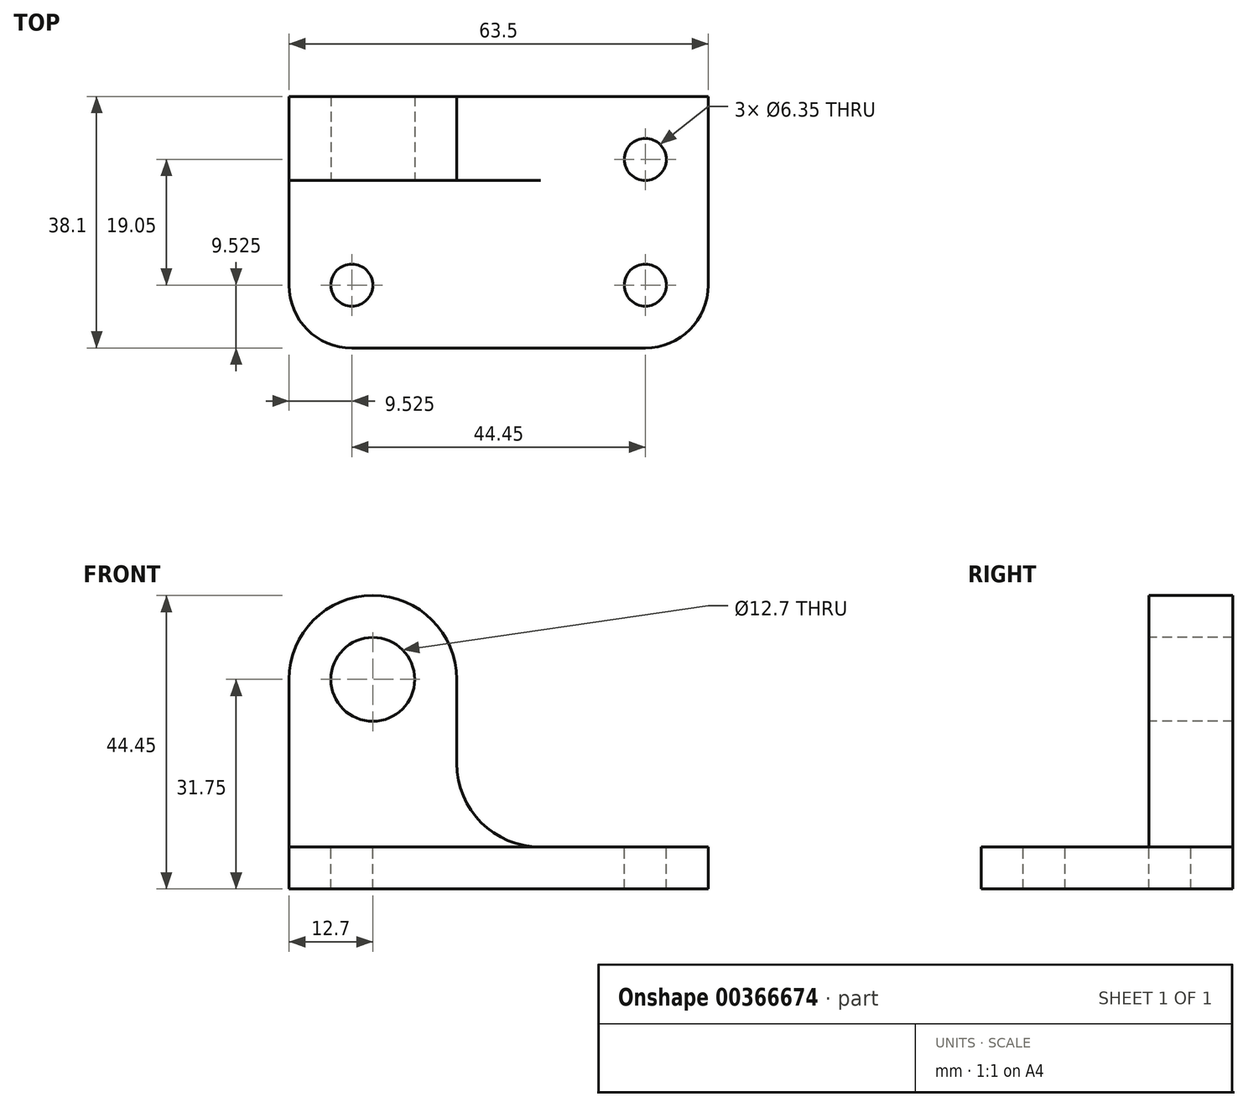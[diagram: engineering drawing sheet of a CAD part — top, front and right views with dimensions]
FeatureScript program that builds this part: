
annotation { "Feature Type Name" : "Feature", "Feature Type Description" : "" }
export const myFeature = defineFeature(function(context is Context, id is Id, definition is map)
    precondition{}
    {
        {
            var Q0;
            Q0=qCreatedBy(makeId("Front.planeOp"),FACE);
            var sketch = newSketch(context, id + "F0", { "sketchPlane" : qUnion([Q0])});
            skLineSegment(sketch, "E0", {"start": v(-70.82, 0) * mm, "end": v(-70.82, 44.45) * mm});
            skLineSegment(sketch, "E1", {"start": v(-70.82, 44.45) * mm, "end": v(-7.32, 44.45) * mm});
            skLineSegment(sketch, "E2", {"start": v(-7.32, 44.45) * mm, "end": v(-7.32, 0) * mm});
            skLineSegment(sketch, "E3", {"start": v(-7.32, 0) * mm, "end": v(-70.82, 0) * mm});
            skSolve(sketch);
        }
        {
            var Q0;
            Q0=makeQuery(id+"F0.imprint","IMPRINT",FACE,{"disambiguationData":[TD([[makeQuery(id+"F0.imprint","IMPRINT",EDGE,{"derivedFrom":sQuery(id+"F0.wireOp",EDGE,"E0")}),-1.0]])]});
            extrude(context, id + "F1", {"entities" : qUnion([Q0]), "depth" : 38.1 * mm});
        }
        {
            var Q0;
            Q0=makeQuery(id+"F1.opExtrude","CAP_FACE",FACE,{"disambiguationData":[OSD([sQuery(id+"F0.wireOp",EDGE,"E0"),sQuery(id+"F0.wireOp",EDGE,"E1"),sQuery(id+"F0.wireOp",EDGE,"E2"),sQuery(id+"F0.wireOp",EDGE,"E3")])],"isStart":false});
            var sketch = newSketch(context, id + "F2", { "sketchPlane" : qUnion([Q0])});
            skLineSegment(sketch, "E4", {"start": v(-70.82, 6.35) * mm, "end": v(-7.32, 6.35) * mm});
            skSolve(sketch);
        }
        {
            var Q0;
            {var subQ0=sQuery(id+"F2.wireOp",EDGE,"E4");Q0=makeQuery(id+"F2.imprint","IMPRINT",FACE,{"disambiguationData":[TD([[makeQuery(id+"F2.imprint","IMPRINT",EDGE,{"derivedFrom":subQ0}),1.0]])]});}
            extrude(context, id + "F3", {"entities" : qUnion([Q0]), "operationType" : NewBodyOperationType.REMOVE, "oppositeDirection" : true, "depth" : 25.4 * mm});
        }
        {
            var Q0;
            Q0=makeQuery(id+"F3.boolean.opBoolean","COPY",FACE,{"derivedFrom":makeQuery(id+"F3.opExtrude","SWEPT_FACE",FACE,{"disambiguationData":[OSD([sQuery(id+"F2.wireOp",EDGE,"E4")])]})});
            var sketch = newSketch(context, id + "F4", { "sketchPlane" : qUnion([Q0])});
            skCircle(sketch, "E5", {"center": v(-61.3, -28.58) * mm, "radius": 3.18 * mm});
            skCircle(sketch, "E6", {"center": v(-16.85, -28.58) * mm, "radius": 3.18 * mm});
            skArc(sketch, "E7", {"start": v(-70.82, -28.58) * mm, "mid": v(-68.03, -35.31) * mm, "end": v(-61.3, -38.1) * mm});
            skArc(sketch, "E8", {"start": v(-16.85, -38.1) * mm, "mid": v(-10.11, -35.3) * mm, "end": v(-7.32, -28.57) * mm});
            skSolve(sketch);
        }
        {
            var Q0;
            {var subQ0=sQuery(id+"F4.wireOp",EDGE,"E7");Q0=makeQuery(id+"F4.imprint","IMPRINT",FACE,{"disambiguationData":[TD([[makeQuery(id+"F4.imprint","IMPRINT",EDGE,{"derivedFrom":subQ0}),-1.0]])]});}
            var Q1;
            Q1=makeQuery(id+"F4.imprint","IMPRINT",FACE,{"disambiguationData":[TD([[makeQuery(id+"F4.imprint","IMPRINT",EDGE,{"derivedFrom":sQuery(id+"F4.wireOp",EDGE,"E5")}),1.0]])]});
            var Q2;
            Q2=makeQuery(id+"F4.imprint","IMPRINT",FACE,{"disambiguationData":[TD([[makeQuery(id+"F4.imprint","IMPRINT",EDGE,{"derivedFrom":sQuery(id+"F4.wireOp",EDGE,"E6")}),1.0]])]});
            var Q3;
            {var subQ0=sQuery(id+"F4.wireOp",EDGE,"E8");Q3=makeQuery(id+"F4.imprint","IMPRINT",FACE,{"disambiguationData":[TD([[makeQuery(id+"F4.imprint","IMPRINT",EDGE,{"derivedFrom":subQ0}),-1.0]])]});}
            extrude(context, id + "F5", {"entities" : qUnion([Q0, Q1, Q2, Q3]), "operationType" : NewBodyOperationType.REMOVE, "oppositeDirection" : true, "depth" : 25.4 * mm});
        }
        {
            var Q0;
            Q0=makeQuery(id+"F3.boolean.opBoolean","COPY",FACE,{"derivedFrom":makeQuery(id+"F3.opExtrude","CAP_FACE",FACE,{"disambiguationData":[OSD([sQuery(id+"F0.wireOp",EDGE,"E0"),sQuery(id+"F0.wireOp",EDGE,"E1"),sQuery(id+"F0.wireOp",EDGE,"E2"),sQuery(id+"F2.wireOp",EDGE,"E4")])],"isStart":false})});
            var sketch = newSketch(context, id + "F6", { "sketchPlane" : qUnion([Q0])});
            skLineSegment(sketch, "E9", {"start": v(-32.72, 6.35) * mm, "end": v(-32.72, 19.05) * mm});
            skLineSegment(sketch, "E10", {"start": v(-32.72, 19.05) * mm, "end": v(-45.42, 19.05) * mm});
            skLineSegment(sketch, "E11", {"start": v(-45.42, 19.05) * mm, "end": v(-45.42, 44.45) * mm});
            skSolve(sketch);
        }
        {
            var Q0;
            {var subQ2=sQuery(id+"F6.wireOp",EDGE,"E9");Q0=makeQuery(id+"F6.imprint","IMPRINT",FACE,{"disambiguationData":[TD([[makeQuery(id+"F6.imprint","IMPRINT",EDGE,{"derivedFrom":subQ2}),-1.0]])]});}
            extrude(context, id + "F7", {"entities" : qUnion([Q0]), "operationType" : NewBodyOperationType.REMOVE, "oppositeDirection" : true, "depth" : 25.4 * mm});
        }
        {
            var Q0;
            Q0=makeQuery(id+"F3.boolean.opBoolean","COPY",FACE,{"derivedFrom":makeQuery(id+"F3.opExtrude","CAP_FACE",FACE,{"disambiguationData":[OSD([sQuery(id+"F0.wireOp",EDGE,"E0"),sQuery(id+"F0.wireOp",EDGE,"E1"),sQuery(id+"F0.wireOp",EDGE,"E2"),sQuery(id+"F2.wireOp",EDGE,"E4")])],"isStart":false})});
            var sketch = newSketch(context, id + "F8", { "sketchPlane" : qUnion([Q0])});
            skArc(sketch, "E12", {"start": v(-45.42, 19.05) * mm, "mid": v(-41.7, 10.07) * mm, "end": v(-32.72, 6.35) * mm});
            skCircle(sketch, "E13", {"center": v(-58.12, 31.75) * mm, "radius": 6.35 * mm});
            skArc(sketch, "E14", {"start": v(-45.42, 31.75) * mm, "mid": v(-58.12, 44.45) * mm, "end": v(-70.82, 31.75) * mm});
            skSolve(sketch);
        }
        {
            var Q0;
            Q0=makeQuery(id+"F8.imprint","IMPRINT",FACE,{"disambiguationData":[TD([[makeQuery(id+"F8.imprint","IMPRINT",EDGE,{"derivedFrom":sQuery(id+"F8.wireOp",EDGE,"E13")}),1.0]])]});
            var Q1;
            {var subQ0=sQuery(id+"F8.wireOp",EDGE,"E14");var subQ1=makeQuery(id+"F7.boolean.opBoolean","COPY",EDGE,{"derivedFrom":makeQuery(id+"F7.opExtrude","CAP_EDGE",EDGE,{"disambiguationData":[OSD([sQuery(id+"F6.wireOp",EDGE,"E11")])],"isStart":true})});var subQ2=makeQuery(id+"F8.imprint","INTERSECT",VERTEX,{"derivedFrom":[subQ1,subQ0]});Q1=makeQuery(id+"F8.imprint","IMPRINT",FACE,{"disambiguationData":[TD([[makeQuery(id+"F8.imprint","IMPRINT",EDGE,{"disambiguationData":[TD([[subQ2,-1.0]])],"derivedFrom":subQ0}),-1.0]])]});}
            var Q2;
            {var subQ0=sQuery(id+"F8.wireOp",EDGE,"E14");var subQ1=makeQuery(id+"F3.boolean.opBoolean","COPY",EDGE,{"derivedFrom":makeQuery(id+"F3.opExtrude","CAP_EDGE",EDGE,{"disambiguationData":[OSD([sQuery(id+"F0.wireOp",EDGE,"E0")])],"isStart":false})});var subQ2=makeQuery(id+"F8.imprint","INTERSECT",VERTEX,{"derivedFrom":[subQ1,subQ0]});Q2=makeQuery(id+"F8.imprint","IMPRINT",FACE,{"disambiguationData":[TD([[makeQuery(id+"F8.imprint","IMPRINT",EDGE,{"disambiguationData":[TD([[subQ2,1.0]])],"derivedFrom":subQ0}),-1.0]])]});}
            var Q3;
            Q3=makeQuery(id+"F8.imprint","IMPRINT",FACE,{"disambiguationData":[TD([[makeQuery(id+"F8.imprint","IMPRINT",EDGE,{"derivedFrom":sQuery(id+"F8.wireOp",EDGE,"E12")}),1.0]])]});
            extrude(context, id + "F9", {"entities" : qUnion([Q0, Q1, Q2, Q3]), "operationType" : NewBodyOperationType.REMOVE, "oppositeDirection" : true, "depth" : 25.4 * mm});
        }
        {
            var Q0;
            {var subQ0=sQuery(id+"F2.wireOp",EDGE,"E4");Q0=makeQuery(id+"F7.boolean.opBoolean","MERGE",FACE,{"derivedFrom":[makeQuery(id+"F3.boolean.opBoolean","COPY",FACE,{"derivedFrom":makeQuery(id+"F3.opExtrude","SWEPT_FACE",FACE,{"disambiguationData":[OSD([subQ0])]})}),makeQuery(id+"F7.opExtrude","SWEPT_FACE",FACE,{"disambiguationData":[OSD([subQ0])]})]});}
            var sketch = newSketch(context, id + "F10", { "sketchPlane" : qUnion([Q0])});
            skCircle(sketch, "E15", {"center": v(-16.85, -9.53) * mm, "radius": 3.18 * mm});
            skSolve(sketch);
        }
        {
            var Q0;
            Q0=makeQuery(id+"F10.imprint","IMPRINT",FACE,{"disambiguationData":[TD([[makeQuery(id+"F10.imprint","IMPRINT",EDGE,{"derivedFrom":sQuery(id+"F10.wireOp",EDGE,"E15")}),1.0]])]});
            extrude(context, id + "F11", {"entities" : qUnion([Q0]), "operationType" : NewBodyOperationType.REMOVE, "oppositeDirection" : true, "depth" : 25.4 * mm});
        }
    });
